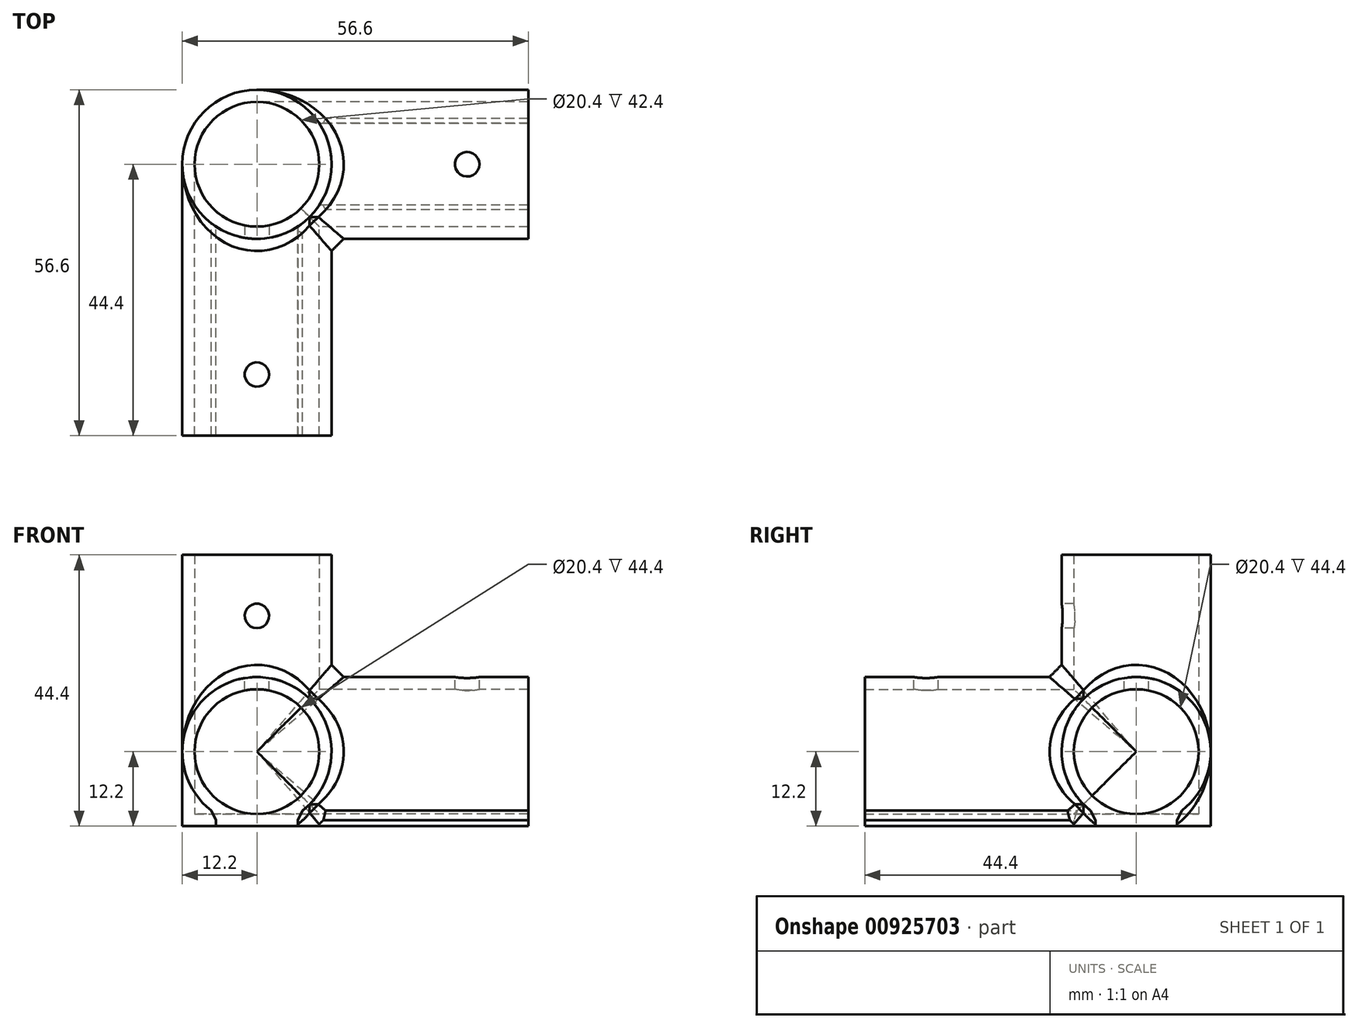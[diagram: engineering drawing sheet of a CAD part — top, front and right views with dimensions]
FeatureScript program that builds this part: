
annotation { "Feature Type Name" : "Feature", "Feature Type Description" : "" }
export const myFeature = defineFeature(function(context is Context, id is Id, definition is map)
    precondition{}
    {
        {
            assignVariable(context, id + "F0", {"name" : "Din", "anyValue" : 20.4 * mm});
        }
        {
            assignVariable(context, id + "F1", {"name" : "Wall", "anyValue" : 2 * mm});
        }
        {
            assignVariable(context, id + "F2", {"name" : "Dout", "anyValue" : getVariable(context, 'Din') + 2 * getVariable(context, 'Wall')});
        }
        {
            assignVariable(context, id + "F3", {"name" : "Ext", "anyValue" : 20 * mm});
        }
        {
            var Q0;
            Q0=qCreatedBy(makeId("Top.planeOp"),FACE);
            var sketch = newSketch(context, id + "F4", { "sketchPlane" : qUnion([Q0])});
            skCircle(sketch, "E0", {"center": v(0, 0) * mm, "radius": 10.2 * mm});
            skCircle(sketch, "E1", {"center": v(0, 0) * mm, "radius": 12.2 * mm});
            skSolve(sketch);
        }
        {
            var Q0;
            Q0=makeQuery(id+"F4.imprint","IMPRINT",FACE,{"disambiguationData":[TD([[makeQuery(id+"F4.imprint","IMPRINT",EDGE,{"derivedFrom":sQuery(id+"F4.wireOp",EDGE,"E0")}),-1.0]])]});
            extrude(context, id + "F5", {"entities" : qUnion([Q0]), "depth" : getVariable(context, 'Dout') + getVariable(context, 'Ext'), "offsetDistance" : 25 * mm});
        }
        {
            var Q0;
            Q0=makeQuery(id+"F4.imprint","IMPRINT",FACE,{"disambiguationData":[TD([[makeQuery(id+"F4.imprint","IMPRINT",EDGE,{"derivedFrom":sQuery(id+"F4.wireOp",EDGE,"E0")}),1.0]])]});
            extrude(context, id + "F6", {"entities" : qUnion([Q0]), "operationType" : NewBodyOperationType.ADD, "depth" : getVariable(context, 'Wall'), "offsetDistance" : 25 * mm});
        }
        {
            var Q0;
            Q0=qCreatedBy(makeId("Front.planeOp"),FACE);
            var sketch = newSketch(context, id + "F7", { "sketchPlane" : qUnion([Q0])});
            skLineSegment(sketch, "E2", {"start": v(0, 0) * mm, "end": v(0, 24.4) * mm, "construction": true});
            skCircle(sketch, "E3", {"center": v(0, 12.2) * mm, "radius": 10.2 * mm});
            skCircle(sketch, "E4", {"center": v(0, 12.2) * mm, "radius": 12.2 * mm});
            skLineSegment(sketch, "E5", {"start": v(12.2, 44.4) * mm, "end": v(12.2, 0) * mm, "construction": true});
            skLineSegment(sketch, "E6", {"start": v(-12.2, 0) * mm, "end": v(-12.2, 44.4) * mm, "construction": true});
            skLineSegment(sketch, "E7", {"start": v(-6.7, 0) * mm, "end": v(-6.7, 2) * mm});
            skLineSegment(sketch, "E8.MirrorCS", {"start": v(6.7, 0) * mm, "end": v(6.7, 2) * mm});
            skLineSegment(sketch, "E9", {"start": v(-6.7, 0) * mm, "end": v(6.7, 0) * mm});
            skLineSegment(sketch, "E10", {"start": v(12.2, 2) * mm, "end": v(-12.2, 2) * mm, "construction": true});
            skSolve(sketch);
        }
        {
            var Q0;
            Q0=makeQuery(id+"F7.imprint","IMPRINT",FACE,{"disambiguationData":[TD([[makeQuery(id+"F7.imprint","IMPRINT",EDGE,{"derivedFrom":sQuery(id+"F7.wireOp",EDGE,"E3")}),-1.0]])]});
            var Q1;
            {var subQ0=sQuery(id+"F7.wireOp",EDGE,"E7");Q1=makeQuery(id+"F7.imprint","IMPRINT",FACE,{"disambiguationData":[TD([[makeQuery(id+"F7.imprint","IMPRINT",EDGE,{"derivedFrom":subQ0}),-1.0]])]});}
            var Q2;
            {var subQ0=sQuery(id+"F7.wireOp",EDGE,"E8.MirrorCS");Q2=makeQuery(id+"F7.imprint","IMPRINT",FACE,{"disambiguationData":[TD([[makeQuery(id+"F7.imprint","IMPRINT",EDGE,{"derivedFrom":subQ0}),1.0]])]});}
            extrude(context, id + "F8", {"entities" : qUnion([Q0, Q1, Q2]), "operationType" : NewBodyOperationType.ADD, "depth" : getVariable(context, 'Dout') + getVariable(context, 'Ext'), "offsetDistance" : 25 * mm});
        }
        {
            var Q0;
            Q0=qCreatedBy(makeId("Right.planeOp"),FACE);
            var sketch = newSketch(context, id + "F9", { "sketchPlane" : qUnion([Q0])});
            skLineSegment(sketch, "E11", {"start": v(0, 0) * mm, "end": v(0, 24.4) * mm, "construction": true});
            skCircle(sketch, "E12", {"center": v(0, 12.2) * mm, "radius": 10.2 * mm});
            skCircle(sketch, "E13", {"center": v(0, 12.2) * mm, "radius": 12.2 * mm});
            skLineSegment(sketch, "E14", {"start": v(-6.7, 0) * mm, "end": v(6.7, 0) * mm});
            skLineSegment(sketch, "E15", {"start": v(-6.7, 0) * mm, "end": v(-6.7, 2) * mm});
            skLineSegment(sketch, "E16.MirrorCS", {"start": v(6.7, 0) * mm, "end": v(6.7, 2) * mm});
            skLineSegment(sketch, "E17", {"start": v(-12.08, 2) * mm, "end": v(12.2, 2) * mm, "construction": true});
            skLineSegment(sketch, "E18", {"start": v(12.2, 44.4) * mm, "end": v(12.2, 0) * mm, "construction": true});
            skLineSegment(sketch, "E19", {"start": v(-12.2, 24.4) * mm, "end": v(-12.2, 44.4) * mm, "construction": true});
            skSolve(sketch);
        }
        {
            var Q0;
            Q0=makeQuery(id+"F9.imprint","IMPRINT",FACE,{"disambiguationData":[TD([[makeQuery(id+"F9.imprint","IMPRINT",EDGE,{"derivedFrom":sQuery(id+"F9.wireOp",EDGE,"E12")}),-1.0]])]});
            var Q1;
            {var subQ0=sQuery(id+"F9.wireOp",EDGE,"E16.MirrorCS");Q1=makeQuery(id+"F9.imprint","IMPRINT",FACE,{"disambiguationData":[TD([[makeQuery(id+"F9.imprint","IMPRINT",EDGE,{"derivedFrom":subQ0}),1.0]])]});}
            var Q2;
            {var subQ0=sQuery(id+"F9.wireOp",EDGE,"E15");Q2=makeQuery(id+"F9.imprint","IMPRINT",FACE,{"disambiguationData":[TD([[makeQuery(id+"F9.imprint","IMPRINT",EDGE,{"derivedFrom":subQ0}),-1.0]])]});}
            extrude(context, id + "F10", {"entities" : qUnion([Q0, Q1, Q2]), "operationType" : NewBodyOperationType.ADD, "depth" : getVariable(context, 'Dout') + getVariable(context, 'Ext'), "offsetDistance" : 25 * mm});
        }
        {
            var Q0;
            Q0=makeQuery(id+"F4.imprint","IMPRINT",FACE,{"disambiguationData":[TD([[makeQuery(id+"F4.imprint","IMPRINT",EDGE,{"derivedFrom":sQuery(id+"F4.wireOp",EDGE,"E0")}),1.0]])]});
            extrude(context, id + "F11", {"entities" : qUnion([Q0]), "operationType" : NewBodyOperationType.REMOVE, "depth" : getVariable(context, 'Dout'), "offsetDistance" : 25 * mm, "hasSecondDirection" : true, "secondDirectionOppositeDirection" : false, "secondDirectionDepth" : getVariable(context, 'Wall')});
        }
        {
            var Q0;
            Q0=makeQuery(id+"F7.imprint","IMPRINT",FACE,{"disambiguationData":[TD([[makeQuery(id+"F7.imprint","IMPRINT",EDGE,{"derivedFrom":sQuery(id+"F7.wireOp",EDGE,"E3")}),1.0]])]});
            var Q1;
            Q1=sQuery(id+"F7.wireOp",EDGE,"E3");
            extrude(context, id + "F12", {"entities" : qUnion([Q0]), "operationType" : NewBodyOperationType.REMOVE, "surfaceEntities" : qUnion([Q1]), "depth" : getVariable(context, 'Dout'), "offsetDistance" : 25 * mm});
        }
        {
            var Q0;
            Q0=makeQuery(id+"F9.imprint","IMPRINT",FACE,{"disambiguationData":[TD([[makeQuery(id+"F9.imprint","IMPRINT",EDGE,{"derivedFrom":sQuery(id+"F9.wireOp",EDGE,"E12")}),1.0]])]});
            extrude(context, id + "F13", {"entities" : qUnion([Q0]), "operationType" : NewBodyOperationType.REMOVE, "depth" : getVariable(context, 'Dout'), "offsetDistance" : 25 * mm});
        }
        {
            var Q0;
            {var subQ0=makeQuery(id+"F5.opExtrude","SWEPT_FACE",FACE,{"disambiguationData":[OSD([sQuery(id+"F4.wireOp",EDGE,"E1")])]});var subQ1=makeQuery(id+"F8.opExtrude","SWEPT_FACE",FACE,{"disambiguationData":[OSD([sQuery(id+"F7.wireOp",EDGE,"E4")])]});Q0=makeQuery(id+"F10.boolean.opBoolean","SPLIT",EDGE,{"disambiguationData":[TD([makeQuery(id+"F10.opExtrude","SWEPT_FACE",FACE,{"disambiguationData":[OSD([sQuery(id+"F9.wireOp",EDGE,"E13")])]})])],"derivedFrom":makeQuery(id+"F8.boolean.opBoolean","INTERSECT",EDGE,{"disambiguationData":[OD(2.0)],"derivedFrom":[subQ0,subQ1]})});}
            var Q1;
            {var subQ0=sQuery(id+"F4.wireOp",EDGE,"E1");var subQ1=sQuery(id+"F4.wireOp",EDGE,"E0");Q1=makeQuery(id+"F10.boolean.opBoolean","INTERSECT",EDGE,{"disambiguationData":[OD(2.0)],"derivedFrom":[makeQuery(id+"F8.boolean.opBoolean","SPLIT",FACE,{"disambiguationData":[TD([makeQuery(id+"F6.opExtrude","CAP_FACE",FACE,{"disambiguationData":[OSD([subQ1])],"isStart":true})])],"derivedFrom":makeQuery(id+"F5.opExtrude","SWEPT_FACE",FACE,{"disambiguationData":[OSD([subQ0])]})}),makeQuery(id+"F10.opExtrude","SWEPT_FACE",FACE,{"disambiguationData":[OSD([sQuery(id+"F9.wireOp",EDGE,"E13")])]})]});}
            var Q2;
            {var subQ0=sQuery(id+"F7.wireOp",EDGE,"E8.MirrorCS");var subQ1=sQuery(id+"F7.wireOp",EDGE,"E7");var subQ2=sQuery(id+"F7.wireOp",EDGE,"E4");Q2=makeQuery(id+"F10.boolean.opBoolean","INTERSECT",EDGE,{"derivedFrom":[makeQuery(id+"F8.boolean.opBoolean","SPLIT",FACE,{"disambiguationData":[TD([makeQuery(id+"F5.opExtrude","SWEPT_FACE",FACE,{"disambiguationData":[OSD([sQuery(id+"F4.wireOp",EDGE,"E1")])]}),makeQuery(id+"F8.opExtrude","CAP_FACE",FACE,{"disambiguationData":[OSD([sQuery(id+"F7.wireOp",EDGE,"E3"),subQ2,subQ1,subQ0,sQuery(id+"F7.wireOp",EDGE,"E9")])],"isStart":false}),makeQuery(id+"F8.opExtrude","SWEPT_FACE",FACE,{"disambiguationData":[OSD([subQ1])]}),makeQuery(id+"F8.opExtrude","SWEPT_FACE",FACE,{"disambiguationData":[OSD([subQ0])]})])],"derivedFrom":makeQuery(id+"F8.opExtrude","SWEPT_FACE",FACE,{"disambiguationData":[OSD([subQ2])]})}),makeQuery(id+"F10.opExtrude","SWEPT_FACE",FACE,{"disambiguationData":[OSD([sQuery(id+"F9.wireOp",EDGE,"E13")])]})]});}
            var Q3;
            {var subQ0=sQuery(id+"F9.wireOp",EDGE,"E13");var subQ1=sQuery(id+"F9.wireOp",EDGE,"E15");Q3=makeQuery(id+"F10.boolean.opBoolean","SPLIT",EDGE,{"disambiguationData":[topologyDisambiguationEdgeConnected([makeQuery(id+"F10.opExtrude","SWEPT_FACE",FACE,{"disambiguationData":[OSD([subQ1])]})])],"derivedFrom":makeQuery(id+"F10.opExtrude","SWEPT_EDGE",EDGE,{"disambiguationData":[OSD([subQ0,subQ1])]})});}
            var Q4;
            {var subQ0=sQuery(id+"F7.wireOp",EDGE,"E4");var subQ1=sQuery(id+"F7.wireOp",EDGE,"E8.MirrorCS");Q4=makeQuery(id+"F8.boolean.opBoolean","SPLIT",EDGE,{"disambiguationData":[topologyDisambiguationEdgeConnected([makeQuery(id+"F8.opExtrude","SWEPT_FACE",FACE,{"disambiguationData":[OSD([subQ1])]})])],"derivedFrom":makeQuery(id+"F8.opExtrude","SWEPT_EDGE",EDGE,{"disambiguationData":[OSD([subQ0,subQ1])]})});}
            var Q5;
            {var subQ0=sQuery(id+"F7.wireOp",EDGE,"E4");var subQ1=sQuery(id+"F7.wireOp",EDGE,"E7");Q5=makeQuery(id+"F8.boolean.opBoolean","SPLIT",EDGE,{"disambiguationData":[topologyDisambiguationEdgeConnected([makeQuery(id+"F8.opExtrude","SWEPT_FACE",FACE,{"disambiguationData":[OSD([subQ1])]})])],"derivedFrom":makeQuery(id+"F8.opExtrude","SWEPT_EDGE",EDGE,{"disambiguationData":[OSD([subQ0,subQ1])]})});}
            var Q6;
            {var subQ0=sQuery(id+"F9.wireOp",EDGE,"E13");var subQ1=sQuery(id+"F9.wireOp",EDGE,"E16.MirrorCS");Q6=makeQuery(id+"F10.boolean.opBoolean","SPLIT",EDGE,{"disambiguationData":[topologyDisambiguationEdgeConnected([makeQuery(id+"F10.opExtrude","SWEPT_FACE",FACE,{"disambiguationData":[OSD([subQ1])]})])],"derivedFrom":makeQuery(id+"F10.opExtrude","SWEPT_EDGE",EDGE,{"disambiguationData":[OSD([subQ0,subQ1])]})});}
            chamfer(context, id + "F14", {"entities" : qUnion([Q0, Q1, Q2, Q3, Q4, Q5, Q6]), "width" : getVariable(context, 'Wall'), "tangentPropagation" : true});
        }
        {
            var Q0;
            Q0=qCreatedBy(makeId("Top.planeOp"),FACE);
            cPlane(context, id + "F15", {"entities" : qUnion([Q0]), "cplaneType" : CPlaneType.OFFSET, "offset" : getVariable(context, 'Dout'), "width" : 150 * mm, "height" : 150 * mm});
        }
        {
            var Q0;
            Q0=qCreatedBy(id+"F15.planeOp",FACE);
            var sketch = newSketch(context, id + "F16", { "sketchPlane" : qUnion([Q0])});
            skLineSegment(sketch, "E20", {"start": v(0, -44.4) * mm, "end": v(0, -34.4) * mm, "construction": true});
            skLineSegment(sketch, "E21", {"start": v(44.4, 0) * mm, "end": v(34.4, 0) * mm, "construction": true});
            skSolve(sketch);
        }
        {
            var Q0;
            Q0=sQuery(id+"F16.wireOp",VERTEX,"E20.end");
            var Q1;
            Q1=sQuery(id+"F16.wireOp",VERTEX,"E21.end");
            var Q2;
            Q2=makeQuery(id+"F5.opExtrude","SWEPT_BODY",BODY,{"disambiguationData":[OSD([sQuery(id+"F4.wireOp",EDGE,"E0"),sQuery(id+"F4.wireOp",EDGE,"E1")])]});
            hole(context, id + "F17", {"style" : HoleStyle.SIMPLE, "endStyle" : HoleEndStyle.BLIND, "holeDiameter" : 4 * mm, "majorDiameter" : 5 * mm, "holeDepth" : getVariable(context, 'Wall'), "isTappedThrough" : true, "tappedDepth" : 12 * mm, "tapClearance" : 3, "locations" : qUnion([Q0, Q1]), "scope" : qUnion([Q2])});
        }
        {
            var Q0;
            Q0=qCreatedBy(makeId("Front.planeOp"),FACE);
            cPlane(context, id + "F18", {"entities" : qUnion([Q0]), "cplaneType" : CPlaneType.OFFSET, "offset" : getVariable(context, 'Dout'), "width" : 150 * mm, "height" : 150 * mm});
        }
        {
            var Q0;
            Q0=qCreatedBy(id+"F18.planeOp",FACE);
            var sketch = newSketch(context, id + "F19", { "sketchPlane" : qUnion([Q0])});
            skLineSegment(sketch, "E22", {"start": v(0, 44.4) * mm, "end": v(0, 34.4) * mm, "construction": true});
            skSolve(sketch);
        }
        {
            var Q0;
            Q0=sQuery(id+"F19.wireOp",VERTEX,"E22.end");
            var Q1;
            Q1=makeQuery(id+"F5.opExtrude","SWEPT_BODY",BODY,{"disambiguationData":[OSD([sQuery(id+"F4.wireOp",EDGE,"E0"),sQuery(id+"F4.wireOp",EDGE,"E1")])]});
            hole(context, id + "F20", {"style" : HoleStyle.SIMPLE, "endStyle" : HoleEndStyle.BLIND, "holeDiameter" : 4 * mm, "majorDiameter" : 5 * mm, "holeDepth" : getVariable(context, 'Wall'), "isTappedThrough" : true, "tappedDepth" : 12 * mm, "tapClearance" : 3, "locations" : qUnion([Q0]), "scope" : qUnion([Q1])});
        }
    });
